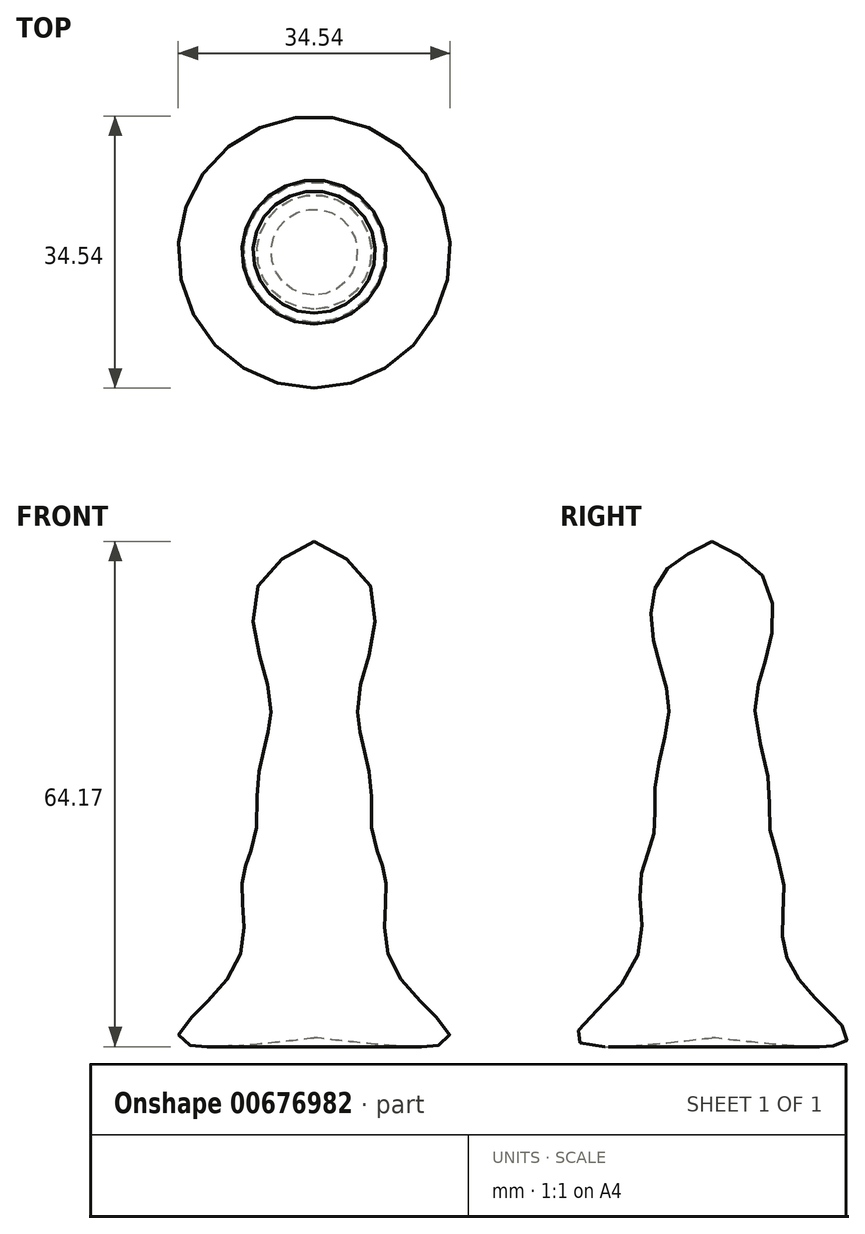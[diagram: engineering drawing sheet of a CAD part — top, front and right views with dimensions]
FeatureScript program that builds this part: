
annotation { "Feature Type Name" : "Feature", "Feature Type Description" : "" }
export const myFeature = defineFeature(function(context is Context, id is Id, definition is map)
    precondition{}
    {
        {
            var Q0;
            Q0=qCreatedBy(makeId("Right.planeOp"),FACE);
            var sketch = newSketch(context, id + "F0", { "sketchPlane" : qUnion([Q0])});
            skFitSpline(sketch, "E0", {"points": [v(0, 63.03) * mm, v(-6.88, 57.97) * mm, v(-7.16, 49.27) * mm, v(-5.47, 41.69) * mm, v(-7.16, 32.7) * mm, v(-7.44, 25.69) * mm, v(-9.12, 19.8) * mm, v(-9.97, 9.12) * mm, v(-17.27, 0) * mm, v(0, 0) * mm], "startDerivative": vector(-79.66, -38.2) * mm, "endDerivative": vector(170.4, 19.65) * mm});
            skFitSpline(sketch, "E1", {"points": [v(-8.53, -0.98) * mm, v(-13.61, -1.13) * mm], "startDerivative": vector(-5.08, -0.15) * mm, "endDerivative": vector(-5.08, -0.15) * mm});
            skLineSegment(sketch, "E2", {"start": v(0, 63.03) * mm, "end": v(0, 0) * mm});
            skSolve(sketch);
        }
        {
            var Q0;
            Q0 = qSketchRegion(id + "F0", true);
            var Q1;
            Q1=sQuery(id+"F0.wireOp",EDGE,"E2");
            revolve(context, id + "F1", {"entities" : qUnion([Q0]), "axis" : qUnion([Q1]), "revolveType" : RevolveType.FULL});
        }
    });
